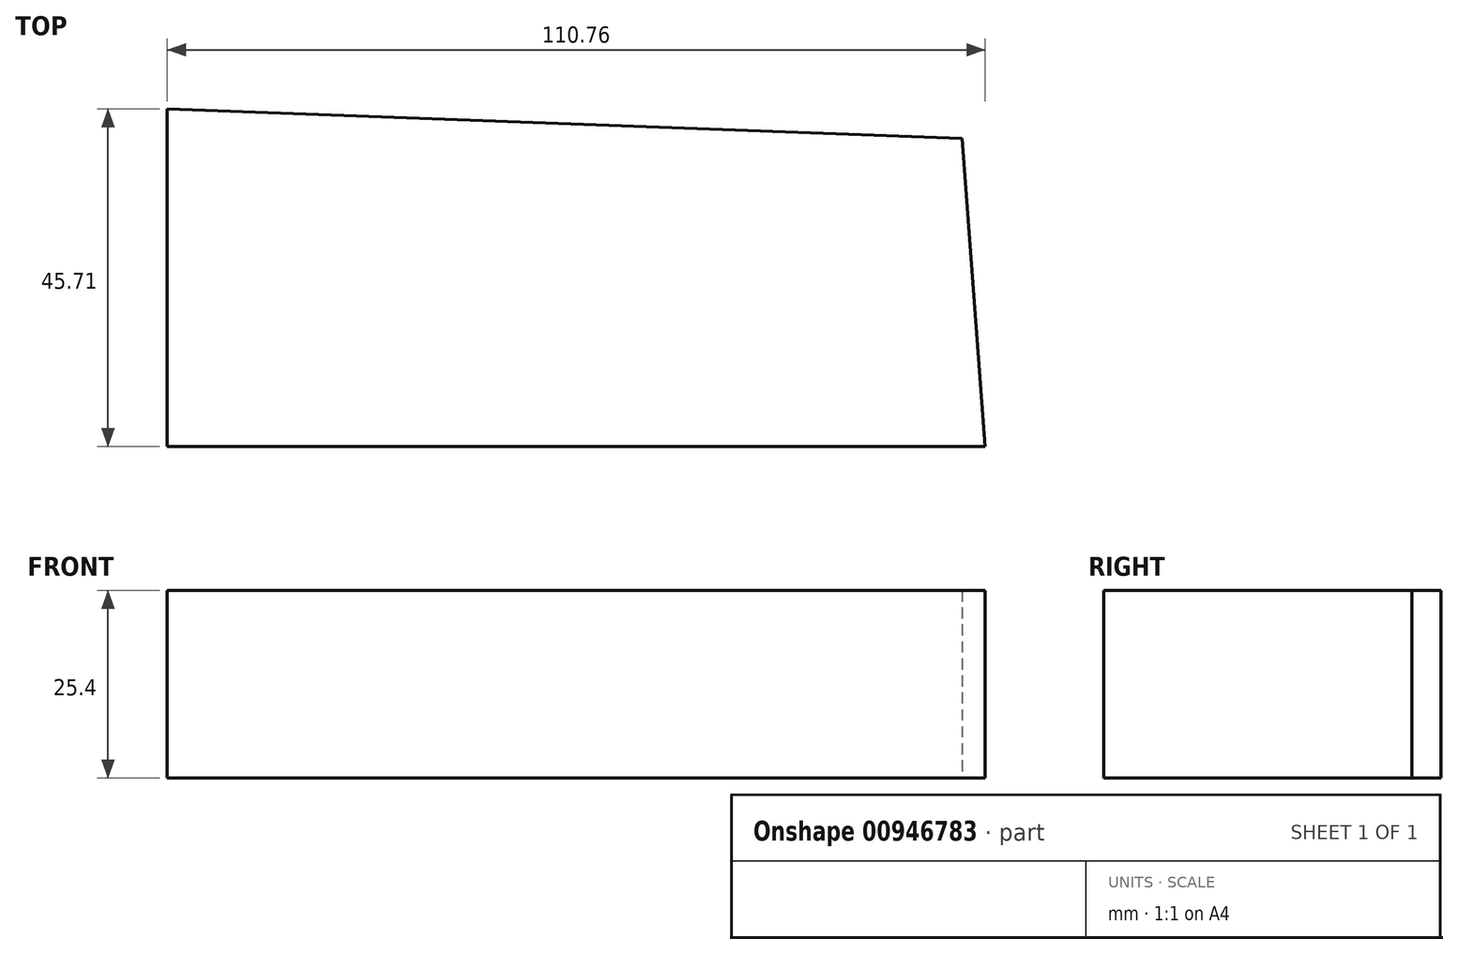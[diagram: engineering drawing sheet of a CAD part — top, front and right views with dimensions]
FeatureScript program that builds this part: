
annotation { "Feature Type Name" : "Feature", "Feature Type Description" : "" }
export const myFeature = defineFeature(function(context is Context, id is Id, definition is map)
    precondition{}
    {
        {
            var Q0;
            Q0=qCreatedBy(makeId("Top.planeOp"),FACE);
            var sketch = newSketch(context, id + "F0", { "sketchPlane" : qUnion([Q0])});
            skLineSegment(sketch, "E0", {"start": v(0, 0) * mm, "end": v(-107.64, 3.97) * mm});
            skLineSegment(sketch, "E1", {"start": v(-107.64, 3.97) * mm, "end": v(-107.64, -41.74) * mm});
            skLineSegment(sketch, "E2", {"start": v(-107.64, -41.74) * mm, "end": v(3.12, -41.74) * mm});
            skLineSegment(sketch, "E3", {"start": v(3.12, -41.74) * mm, "end": v(0, 0) * mm});
            skSolve(sketch);
        }
        {
            var Q0;
            Q0=makeQuery(id+"F0.imprint","IMPRINT",FACE,{"disambiguationData":[TD([[makeQuery(id+"F0.imprint","IMPRINT",EDGE,{"derivedFrom":sQuery(id+"F0.wireOp",EDGE,"E0")}),1.0]])]});
            extrude(context, id + "F1", {"entities" : qUnion([Q0]), "depth" : 25.4 * mm, "offsetDistance" : 25.4 * mm});
        }
    });
